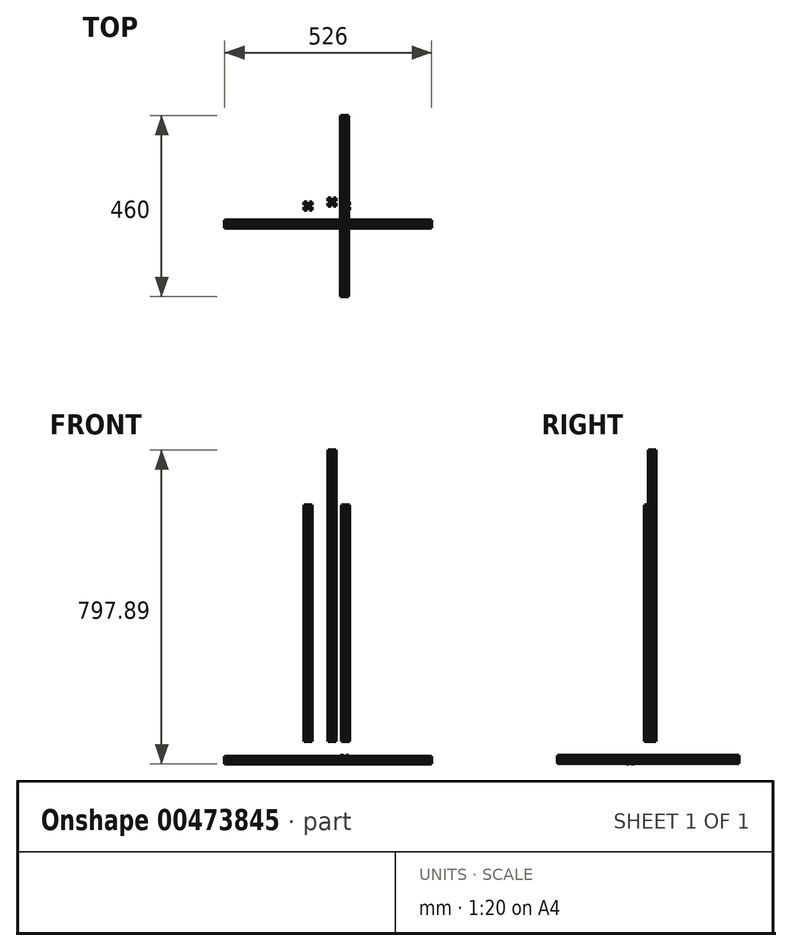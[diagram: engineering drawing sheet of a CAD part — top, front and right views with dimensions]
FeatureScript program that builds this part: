
annotation { "Feature Type Name" : "Feature", "Feature Type Description" : "" }
export const myFeature = defineFeature(function(context is Context, id is Id, definition is map)
    precondition{}
    {
        {
            var Q0;
            Q0=qCreatedBy(makeId("Top.planeOp"),FACE);
            var sketch = newSketch(context, id + "F0", { "sketchPlane" : qUnion([Q0])});
            skLineSegment(sketch, "E0.bottom", {"start": v(0, 0) * mm, "end": v(20, 0) * mm});
            skLineSegment(sketch, "E0.top", {"start": v(0, 20) * mm, "end": v(20, 20) * mm});
            skLineSegment(sketch, "E0.left", {"start": v(0, 0) * mm, "end": v(0, 20) * mm});
            skLineSegment(sketch, "E0.right", {"start": v(20, 0) * mm, "end": v(20, 20) * mm});
            skLineSegment(sketch, "E1.bottom", {"start": v(7, 20) * mm, "end": v(13, 20) * mm});
            skLineSegment(sketch, "E1.top", {"start": v(7, 14.5) * mm, "end": v(13, 14.5) * mm});
            skLineSegment(sketch, "E1.left", {"start": v(7, 20) * mm, "end": v(7, 14.5) * mm});
            skLineSegment(sketch, "E1.right", {"start": v(13, 20) * mm, "end": v(13, 14.5) * mm});
            skLineSegment(sketch, "E2.bottom", {"start": v(20, 13) * mm, "end": v(14.5, 13) * mm});
            skLineSegment(sketch, "E2.top", {"start": v(20, 7) * mm, "end": v(14.5, 7) * mm});
            skLineSegment(sketch, "E2.left", {"start": v(20, 13) * mm, "end": v(20, 7) * mm});
            skLineSegment(sketch, "E2.right", {"start": v(14.5, 13) * mm, "end": v(14.5, 7) * mm});
            skLineSegment(sketch, "E3.bottom", {"start": v(13, 0) * mm, "end": v(7, 0) * mm});
            skLineSegment(sketch, "E3.top", {"start": v(13, 5.5) * mm, "end": v(7, 5.5) * mm});
            skLineSegment(sketch, "E3.left", {"start": v(13, 0) * mm, "end": v(13, 5.5) * mm});
            skLineSegment(sketch, "E3.right", {"start": v(7, 0) * mm, "end": v(7, 5.5) * mm});
            skLineSegment(sketch, "E4.bottom", {"start": v(0, 7) * mm, "end": v(5.5, 7) * mm});
            skLineSegment(sketch, "E4.top", {"start": v(0, 13) * mm, "end": v(5.5, 13) * mm});
            skLineSegment(sketch, "E4.left", {"start": v(0, 7) * mm, "end": v(0, 13) * mm});
            skLineSegment(sketch, "E4.right", {"start": v(5.5, 7) * mm, "end": v(5.5, 13) * mm});
            skSolve(sketch);
        }
        {
            var Q0;
            Q0=makeQuery(id+"F0.imprint","IMPRINT",FACE,{"disambiguationData":[TD([[makeQuery(id+"F0.imprint","IMPRINT",EDGE,{"derivedFrom":sQuery(id+"F0.wireOp",EDGE,"E1.top")}),-1.0]])]});
            extrude(context, id + "F1", {"entities" : qUnion([Q0]), "depth" : 740 * mm});
        }
        {
            var Q0;
            Q0=qCreatedBy(makeId("Top.planeOp"),FACE);
            var sketch = newSketch(context, id + "F2", { "sketchPlane" : qUnion([Q0])});
            skLineSegment(sketch, "E5.bottom", {"start": v(-61, -10) * mm, "end": v(-41, -10) * mm});
            skLineSegment(sketch, "E5.top", {"start": v(-61, 10) * mm, "end": v(-41, 10) * mm});
            skLineSegment(sketch, "E5.left", {"start": v(-61, -10) * mm, "end": v(-61, 10) * mm});
            skLineSegment(sketch, "E5.right", {"start": v(-41, -10) * mm, "end": v(-41, 10) * mm});
            skLineSegment(sketch, "E6.top", {"start": v(-54, 4.5) * mm, "end": v(-48, 4.5) * mm});
            skLineSegment(sketch, "E6.left", {"start": v(-54, 10) * mm, "end": v(-54, 4.5) * mm});
            skLineSegment(sketch, "E6.right", {"start": v(-48, 10) * mm, "end": v(-48, 4.5) * mm});
            skLineSegment(sketch, "E7.bottom", {"start": v(-41, 3) * mm, "end": v(-46.5, 3) * mm});
            skLineSegment(sketch, "E7.top", {"start": v(-41, -3) * mm, "end": v(-46.5, -3) * mm});
            skLineSegment(sketch, "E7.left", {"start": v(-41, 3) * mm, "end": v(-41, -3) * mm});
            skLineSegment(sketch, "E7.right", {"start": v(-46.5, 3) * mm, "end": v(-46.5, -3) * mm});
            skLineSegment(sketch, "E8.top", {"start": v(-48, -4.5) * mm, "end": v(-54, -4.5) * mm});
            skLineSegment(sketch, "E8.left", {"start": v(-48, -10) * mm, "end": v(-48, -4.5) * mm});
            skLineSegment(sketch, "E8.right", {"start": v(-54, -10) * mm, "end": v(-54, -4.5) * mm});
            skLineSegment(sketch, "E9.bottom", {"start": v(-61, -3) * mm, "end": v(-55.5, -3) * mm});
            skLineSegment(sketch, "E9.top", {"start": v(-61, 3) * mm, "end": v(-55.5, 3) * mm});
            skLineSegment(sketch, "E9.left", {"start": v(-61, -3) * mm, "end": v(-61, 3) * mm});
            skLineSegment(sketch, "E9.right", {"start": v(-55.5, -3) * mm, "end": v(-55.5, 3) * mm});
            skSolve(sketch);
        }
        {
            var Q0;
            Q0=makeQuery(id+"F2.imprint","IMPRINT",FACE,{"disambiguationData":[TD([[makeQuery(id+"F2.imprint","IMPRINT",EDGE,{"derivedFrom":sQuery(id+"F2.wireOp",EDGE,"E6.top")}),-1.0]])]});
            extrude(context, id + "F3", {"entities" : qUnion([Q0]), "depth" : 600 * mm});
        }
        {
            var Q0;
            Q0=qCreatedBy(makeId("Top.planeOp"),FACE);
            var sketch = newSketch(context, id + "F4", { "sketchPlane" : qUnion([Q0])});
            skLineSegment(sketch, "E10.bottom", {"start": v(34, -10) * mm, "end": v(54, -10) * mm});
            skLineSegment(sketch, "E10.top", {"start": v(34, 10) * mm, "end": v(54, 10) * mm});
            skLineSegment(sketch, "E10.left", {"start": v(34, -10) * mm, "end": v(34, 10) * mm});
            skLineSegment(sketch, "E10.right", {"start": v(54, -10) * mm, "end": v(54, 10) * mm});
            skLineSegment(sketch, "E11.bottom", {"start": v(41, 10) * mm, "end": v(47, 10) * mm});
            skLineSegment(sketch, "E11.top", {"start": v(41, 4.5) * mm, "end": v(47, 4.5) * mm});
            skLineSegment(sketch, "E11.left", {"start": v(41, 10) * mm, "end": v(41, 4.5) * mm});
            skLineSegment(sketch, "E11.right", {"start": v(47, 10) * mm, "end": v(47, 4.5) * mm});
            skLineSegment(sketch, "E12.bottom", {"start": v(54, 3) * mm, "end": v(48.5, 3) * mm});
            skLineSegment(sketch, "E12.top", {"start": v(54, -3) * mm, "end": v(48.5, -3) * mm});
            skLineSegment(sketch, "E12.left", {"start": v(54, 3) * mm, "end": v(54, -3) * mm});
            skLineSegment(sketch, "E12.right", {"start": v(48.5, 3) * mm, "end": v(48.5, -3) * mm});
            skLineSegment(sketch, "E13.bottom", {"start": v(47, -10) * mm, "end": v(41, -10) * mm});
            skLineSegment(sketch, "E13.top", {"start": v(47, -4.5) * mm, "end": v(41, -4.5) * mm});
            skLineSegment(sketch, "E13.left", {"start": v(47, -10) * mm, "end": v(47, -4.5) * mm});
            skLineSegment(sketch, "E13.right", {"start": v(41, -10) * mm, "end": v(41, -4.5) * mm});
            skLineSegment(sketch, "E14.bottom", {"start": v(34, -3) * mm, "end": v(39.5, -3) * mm});
            skLineSegment(sketch, "E14.top", {"start": v(34, 3) * mm, "end": v(39.5, 3) * mm});
            skLineSegment(sketch, "E14.left", {"start": v(34, -3) * mm, "end": v(34, 3) * mm});
            skLineSegment(sketch, "E14.right", {"start": v(39.5, -3) * mm, "end": v(39.5, 3) * mm});
            skSolve(sketch);
        }
        {
            var Q0;
            Q0=makeQuery(id+"F4.imprint","IMPRINT",FACE,{"disambiguationData":[TD([[makeQuery(id+"F4.imprint","IMPRINT",EDGE,{"derivedFrom":sQuery(id+"F4.wireOp",EDGE,"E11.top")}),-1.0]])]});
            extrude(context, id + "F5", {"entities" : qUnion([Q0]), "depth" : 600 * mm});
        }
        {
            var Q0;
            Q0=qCreatedBy(makeId("Right.planeOp"),FACE);
            var sketch = newSketch(context, id + "F6", { "sketchPlane" : qUnion([Q0])});
            skLineSegment(sketch, "E15.bottom", {"start": v(-55.88, -57.89) * mm, "end": v(-35.88, -57.89) * mm});
            skLineSegment(sketch, "E15.top", {"start": v(-55.88, -37.89) * mm, "end": v(-35.88, -37.89) * mm});
            skLineSegment(sketch, "E15.left", {"start": v(-55.88, -57.89) * mm, "end": v(-55.88, -37.89) * mm});
            skLineSegment(sketch, "E15.right", {"start": v(-35.88, -57.89) * mm, "end": v(-35.88, -37.89) * mm});
            skLineSegment(sketch, "E16.bottom", {"start": v(-48.88, -37.89) * mm, "end": v(-42.88, -37.89) * mm});
            skLineSegment(sketch, "E16.top", {"start": v(-48.88, -43.39) * mm, "end": v(-42.88, -43.39) * mm});
            skLineSegment(sketch, "E16.left", {"start": v(-48.88, -37.89) * mm, "end": v(-48.88, -43.39) * mm});
            skLineSegment(sketch, "E16.right", {"start": v(-42.88, -37.89) * mm, "end": v(-42.88, -43.39) * mm});
            skLineSegment(sketch, "E17.bottom", {"start": v(-35.88, -44.89) * mm, "end": v(-41.38, -44.89) * mm});
            skLineSegment(sketch, "E17.top", {"start": v(-35.88, -50.89) * mm, "end": v(-41.38, -50.89) * mm});
            skLineSegment(sketch, "E17.left", {"start": v(-35.88, -44.89) * mm, "end": v(-35.88, -50.89) * mm});
            skLineSegment(sketch, "E17.right", {"start": v(-41.38, -44.89) * mm, "end": v(-41.38, -50.89) * mm});
            skLineSegment(sketch, "E18.bottom", {"start": v(-42.88, -57.89) * mm, "end": v(-48.88, -57.89) * mm});
            skLineSegment(sketch, "E18.top", {"start": v(-42.88, -52.39) * mm, "end": v(-48.88, -52.39) * mm});
            skLineSegment(sketch, "E18.left", {"start": v(-42.88, -57.89) * mm, "end": v(-42.88, -52.39) * mm});
            skLineSegment(sketch, "E18.right", {"start": v(-48.88, -57.89) * mm, "end": v(-48.88, -52.39) * mm});
            skLineSegment(sketch, "E19.bottom", {"start": v(-55.88, -50.89) * mm, "end": v(-50.38, -50.89) * mm});
            skLineSegment(sketch, "E19.top", {"start": v(-55.88, -44.89) * mm, "end": v(-50.38, -44.89) * mm});
            skLineSegment(sketch, "E19.left", {"start": v(-55.88, -50.89) * mm, "end": v(-55.88, -44.89) * mm});
            skLineSegment(sketch, "E19.right", {"start": v(-50.38, -50.89) * mm, "end": v(-50.38, -44.89) * mm});
            skSolve(sketch);
        }
        {
            var Q0;
            Q0=makeQuery(id+"F6.imprint","IMPRINT",FACE,{"disambiguationData":[TD([[makeQuery(id+"F6.imprint","IMPRINT",EDGE,{"derivedFrom":sQuery(id+"F6.wireOp",EDGE,"E16.top")}),-1.0]])]});
            extrude(context, id + "F7", {"entities" : qUnion([Q0]), "depth" : 526 * mm, "symmetric" : true});
        }
        {
            var Q0;
            Q0=qCreatedBy(makeId("Front.planeOp"),FACE);
            var sketch = newSketch(context, id + "F8", { "sketchPlane" : qUnion([Q0])});
            skLineSegment(sketch, "E20.bottom", {"start": v(31.6, -56.3) * mm, "end": v(51.6, -56.3) * mm});
            skLineSegment(sketch, "E20.top", {"start": v(31.6, -36.3) * mm, "end": v(51.6, -36.3) * mm});
            skLineSegment(sketch, "E20.left", {"start": v(31.6, -56.3) * mm, "end": v(31.6, -36.3) * mm});
            skLineSegment(sketch, "E20.right", {"start": v(51.6, -56.3) * mm, "end": v(51.6, -36.3) * mm});
            skLineSegment(sketch, "E21.bottom", {"start": v(38.6, -36.3) * mm, "end": v(44.6, -36.3) * mm});
            skLineSegment(sketch, "E21.top", {"start": v(38.6, -41.8) * mm, "end": v(44.6, -41.8) * mm});
            skLineSegment(sketch, "E21.left", {"start": v(38.6, -36.3) * mm, "end": v(38.6, -41.8) * mm});
            skLineSegment(sketch, "E21.right", {"start": v(44.6, -36.3) * mm, "end": v(44.6, -41.8) * mm});
            skLineSegment(sketch, "E22.bottom", {"start": v(51.6, -43.3) * mm, "end": v(46.1, -43.3) * mm});
            skLineSegment(sketch, "E22.top", {"start": v(51.6, -49.3) * mm, "end": v(46.1, -49.3) * mm});
            skLineSegment(sketch, "E22.left", {"start": v(51.6, -43.3) * mm, "end": v(51.6, -49.3) * mm});
            skLineSegment(sketch, "E22.right", {"start": v(46.1, -43.3) * mm, "end": v(46.1, -49.3) * mm});
            skLineSegment(sketch, "E23.bottom", {"start": v(44.6, -56.3) * mm, "end": v(38.6, -56.3) * mm});
            skLineSegment(sketch, "E23.top", {"start": v(44.6, -50.8) * mm, "end": v(38.6, -50.8) * mm});
            skLineSegment(sketch, "E23.left", {"start": v(44.6, -56.3) * mm, "end": v(44.6, -50.8) * mm});
            skLineSegment(sketch, "E23.right", {"start": v(38.6, -56.3) * mm, "end": v(38.6, -50.8) * mm});
            skLineSegment(sketch, "E24.bottom", {"start": v(31.6, -49.3) * mm, "end": v(37.1, -49.3) * mm});
            skLineSegment(sketch, "E24.top", {"start": v(31.6, -43.3) * mm, "end": v(37.1, -43.3) * mm});
            skLineSegment(sketch, "E24.left", {"start": v(31.6, -49.3) * mm, "end": v(31.6, -43.3) * mm});
            skLineSegment(sketch, "E24.right", {"start": v(37.1, -49.3) * mm, "end": v(37.1, -43.3) * mm});
            skSolve(sketch);
        }
        {
            var Q0;
            Q0=makeQuery(id+"F8.imprint","IMPRINT",FACE,{"disambiguationData":[TD([[makeQuery(id+"F8.imprint","IMPRINT",EDGE,{"derivedFrom":sQuery(id+"F8.wireOp",EDGE,"E21.top")}),-1.0]])]});
            extrude(context, id + "F9", {"entities" : qUnion([Q0]), "depth" : 460 * mm, "symmetric" : true});
        }
    });
